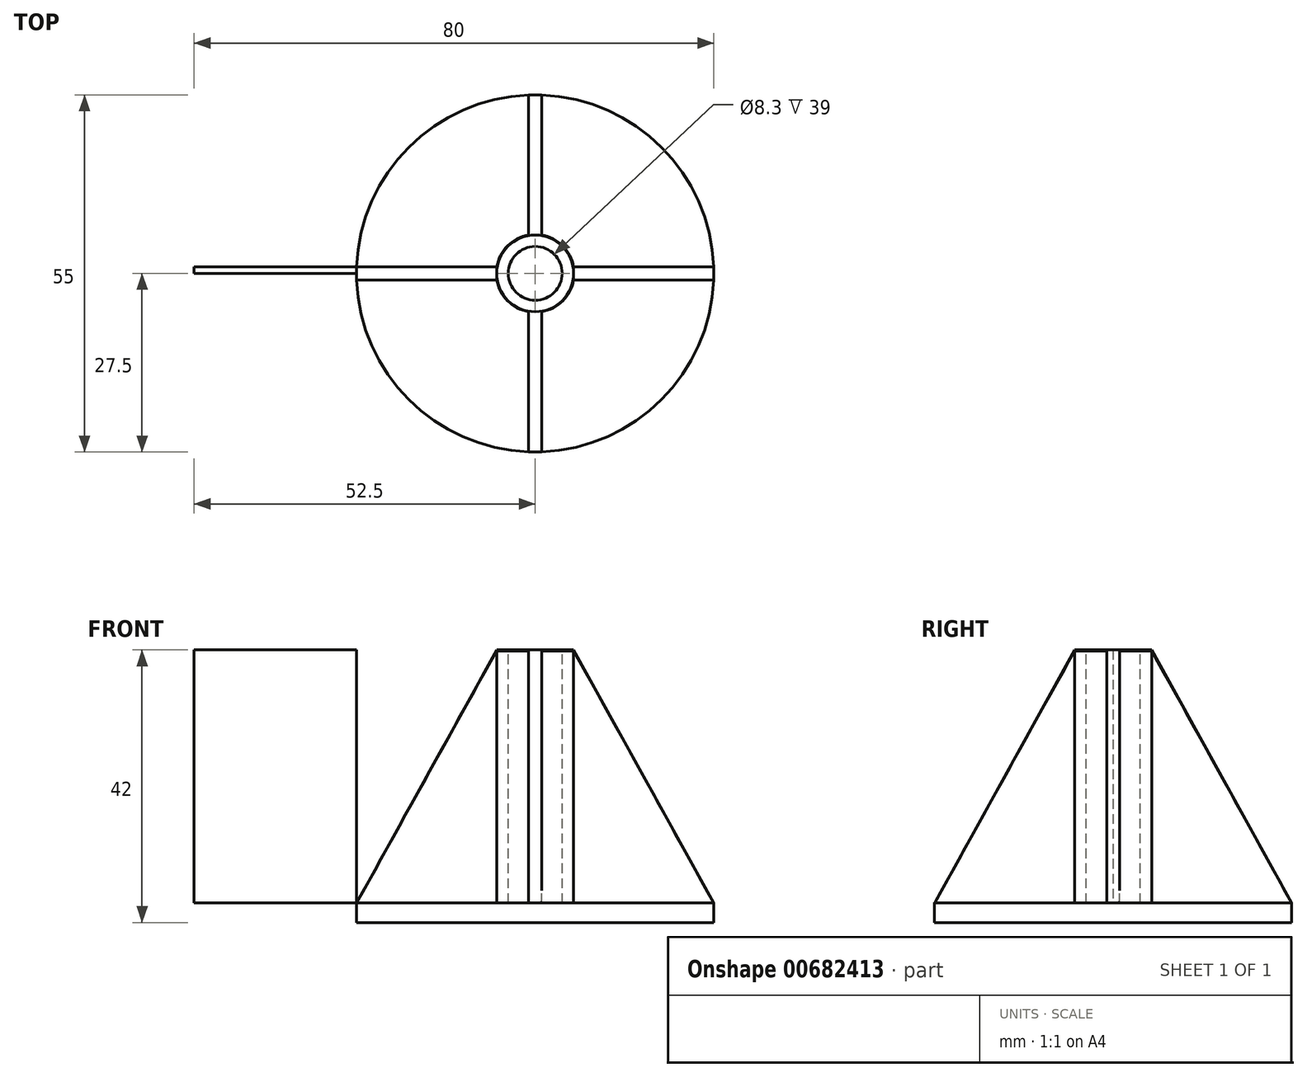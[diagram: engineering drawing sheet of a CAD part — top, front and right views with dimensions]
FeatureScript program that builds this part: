
annotation { "Feature Type Name" : "Feature", "Feature Type Description" : "" }
export const myFeature = defineFeature(function(context is Context, id is Id, definition is map)
    precondition{}
    {
        {
            var Q0;
            Q0=qCreatedBy(makeId("Top.planeOp"),FACE);
            var sketch = newSketch(context, id + "F0", { "sketchPlane" : qUnion([Q0])});
            skCircle(sketch, "E0", {"center": v(-3.3, 0) * mm, "radius": 27.5 * mm});
            skCircle(sketch, "E1", {"center": v(-3.3, 0) * mm, "radius": 26.5 * mm});
            skSolve(sketch);
        }
        {
            var Q0;
            Q0 = qSketchRegion(id + "F0", true);
            extrude(context, id + "F1", {"entities" : qUnion([Q0]), "depth" : 10 * mm, "offsetDistance" : 25 * mm});
        }
        {
            var Q0;
            Q0=makeQuery(id+"F1.opExtrude","CAP_FACE",FACE,{"disambiguationData":[OSD([sQuery(id+"F0.wireOp",EDGE,"E0"),sQuery(id+"F0.wireOp",EDGE,"E1")])],"isStart":false});
            var sketch = newSketch(context, id + "F2", { "sketchPlane" : qUnion([Q0])});
            skLineSegment(sketch, "E2", {"start": v(-30.8, 0) * mm, "end": v(24.2, 0) * mm});
            skCircle(sketch, "E3", {"center": v(-3.3, 0) * mm, "radius": 27.5 * mm});
            skSolve(sketch);
        }
        {
            var Q0;
            Q0 = qSketchRegion(id + "F2", true);
            extrude(context, id + "F3", {"entities" : qUnion([Q0]), "operationType" : NewBodyOperationType.ADD, "depth" : 3 * mm, "offsetDistance" : 25 * mm});
        }
        {
            var Q0;
            Q0=makeQuery(id+"F3.opExtrude","CAP_FACE",FACE,{"disambiguationData":[OSD([sQuery(id+"F2.wireOp",EDGE,"E3")])],"isStart":false});
            var sketch = newSketch(context, id + "F4", { "sketchPlane" : qUnion([Q0])});
            skCircle(sketch, "E4", {"center": v(-3.3, 0) * mm, "radius": 6 * mm});
            skSolve(sketch);
        }
        {
            var Q0;
            Q0 = qSketchRegion(id + "F4", true);
            extrude(context, id + "F5", {"entities" : qUnion([Q0]), "operationType" : NewBodyOperationType.ADD, "depth" : 39 * mm, "offsetDistance" : 25 * mm});
        }
        {
            var Q0;
            Q0=makeQuery(id+"F5.opExtrude","CAP_FACE",FACE,{"disambiguationData":[OSD([sQuery(id+"F4.wireOp",EDGE,"E4")])],"isStart":false});
            var sketch = newSketch(context, id + "F6", { "sketchPlane" : qUnion([Q0])});
            skCircle(sketch, "E5", {"center": v(-3.3, 0) * mm, "radius": 4.15 * mm});
            skSolve(sketch);
        }
        {
            var Q0;
            Q0 = qSketchRegion(id + "F6", true);
            extrude(context, id + "F7", {"entities" : qUnion([Q0]), "operationType" : NewBodyOperationType.REMOVE, "oppositeDirection" : true, "depth" : 39 * mm, "offsetDistance" : 25 * mm});
        }
        {
            var Q0;
            Q0=makeQuery(id+"F3.opExtrude","CAP_FACE",FACE,{"disambiguationData":[OSD([sQuery(id+"F2.wireOp",EDGE,"E3")])],"isStart":false});
            var sketch = newSketch(context, id + "F8", { "sketchPlane" : qUnion([Q0])});
            skLineSegment(sketch, "E6", {"start": v(-3.3, 0) * mm, "end": v(-3.3, -27.5) * mm});
            skLineSegment(sketch, "E7", {"start": v(-3.3, -27.5) * mm, "end": v(-2.3, -27.5) * mm});
            skLineSegment(sketch, "E8", {"start": v(-2.3, -27.5) * mm, "end": v(-2.3, -5.14) * mm});
            skLineSegment(sketch, "E9", {"start": v(-2.3, -5.14) * mm, "end": v(-4.3, -5.14) * mm});
            skLineSegment(sketch, "E10", {"start": v(-4.3, -5.14) * mm, "end": v(-4.3, -27.48) * mm});
            skLineSegment(sketch, "E11", {"start": v(-4.3, -27.48) * mm, "end": v(-3.3, -27.5) * mm});
            skLineSegment(sketch, "E12.1.0", {"start": v(24.2, 1) * mm, "end": v(1.83, 1) * mm});
            skLineSegment(sketch, "E12.1.1", {"start": v(1.83, 1) * mm, "end": v(1.83, -1) * mm});
            skLineSegment(sketch, "E12.1.2", {"start": v(1.83, -1) * mm, "end": v(24.17, -1) * mm});
            skLineSegment(sketch, "E12.1.3", {"start": v(24.17, -1) * mm, "end": v(24.2, 0) * mm});
            skLineSegment(sketch, "E12.1.4", {"start": v(24.2, 0) * mm, "end": v(24.2, 1) * mm});
            skLineSegment(sketch, "E12.2.0", {"start": v(-4.3, 27.5) * mm, "end": v(-4.3, 5.14) * mm});
            skLineSegment(sketch, "E12.2.1", {"start": v(-4.3, 5.14) * mm, "end": v(-2.3, 5.14) * mm});
            skLineSegment(sketch, "E12.2.2", {"start": v(-2.3, 5.14) * mm, "end": v(-2.3, 27.48) * mm});
            skLineSegment(sketch, "E12.2.3", {"start": v(-2.3, 27.48) * mm, "end": v(-3.3, 27.5) * mm});
            skLineSegment(sketch, "E12.2.4", {"start": v(-3.3, 27.5) * mm, "end": v(-4.3, 27.5) * mm});
            skLineSegment(sketch, "E12.3.0", {"start": v(-30.8, -1) * mm, "end": v(-8.45, -1) * mm});
            skLineSegment(sketch, "E12.3.1", {"start": v(-8.45, -1) * mm, "end": v(-8.45, 1) * mm});
            skLineSegment(sketch, "E12.3.2", {"start": v(-8.45, 1) * mm, "end": v(-30.8, 1) * mm});
            skLineSegment(sketch, "E12.3.3", {"start": v(-30.8, 1) * mm, "end": v(-30.8, 0) * mm});
            skLineSegment(sketch, "E12.3.4", {"start": v(-30.8, 0) * mm, "end": v(-30.8, -1) * mm});
            skPoint(sketch, "E12.center", {"position": v(-3.3, 0) * mm});
            skSolve(sketch);
        }
        {
            var Q0;
            Q0 = qSketchRegion(id + "F8", true);
            extrude(context, id + "F9", {"entities" : qUnion([Q0]), "operationType" : NewBodyOperationType.ADD, "depth" : 39 * mm, "offsetDistance" : 25 * mm});
        }
        {
            var Q0;
            Q0=makeQuery(id+"F9.opExtrude","SWEPT_FACE",FACE,{"disambiguationData":[OSD([sQuery(id+"F8.wireOp",EDGE,"E12.3.4")])]});
            var sketch = newSketch(context, id + "F10", { "sketchPlane" : qUnion([Q0])});
            skLineSegment(sketch, "E13", {"start": v(0, 52) * mm, "end": v(0, 13) * mm});
            skLineSegment(sketch, "E14", {"start": v(0, 13) * mm, "end": v(-0.99, 13) * mm});
            skLineSegment(sketch, "E15", {"start": v(-0.99, 13) * mm, "end": v(-0.99, 52) * mm});
            skLineSegment(sketch, "E16", {"start": v(-0.99, 52) * mm, "end": v(0, 52) * mm});
            skSolve(sketch);
        }
        {
            var Q0;
            Q0 = qSketchRegion(id + "F10", true);
            extrude(context, id + "F11", {"entities" : qUnion([Q0]), "depth" : 25 * mm, "offsetDistance" : 25 * mm});
        }
        {
            var Q0;
            Q0=makeQuery(id+"F11.opExtrude","SWEPT_FACE",FACE,{"disambiguationData":[OSD([sQuery(id+"F10.wireOp",EDGE,"E13")])]});
            var sketch = newSketch(context, id + "F12", { "sketchPlane" : qUnion([Q0])});
            skLineSegment(sketch, "E17", {"start": v(-30.8, 13) * mm, "end": v(24.2, 13) * mm});
            skLineSegment(sketch, "E18", {"start": v(24.2, 13) * mm, "end": v(32.46, 54.61) * mm});
            skLineSegment(sketch, "E19", {"start": v(32.46, 54.61) * mm, "end": v(1.97, 54.61) * mm});
            skLineSegment(sketch, "E20", {"start": v(1.97, 54.61) * mm, "end": v(2.6, 52) * mm});
            skLineSegment(sketch, "E21", {"start": v(2.6, 52) * mm, "end": v(24.2, 13) * mm});
            skLineSegment(sketch, "E22", {"start": v(-3.3, 13) * mm, "end": v(-3.3, 60.1) * mm});
            skSolve(sketch);
        }
        {
            var Q0;
            Q0=makeQuery(id+"F12.imprint","IMPRINT",FACE,{"disambiguationData":[TD([[makeQuery(id+"F12.imprint","IMPRINT",EDGE,{"derivedFrom":sQuery(id+"F12.wireOp",EDGE,"E18")}),1.0]])]});
            var Q1;
            Q1=sQuery(id+"F12.wireOp",EDGE,"E22");
            revolve(context, id + "F13", {"entities" : qUnion([Q0]), "axis" : qUnion([Q1]), "revolveType" : RevolveType.FULL});
        }
        {
            var Q0;
            Q0=makeQuery(id+"F13.opRevolve","SWEPT_BODY",BODY,{"disambiguationData":[OSD([sQuery(id+"F12.wireOp",EDGE,"E18"),sQuery(id+"F12.wireOp",EDGE,"E19"),sQuery(id+"F12.wireOp",EDGE,"E20"),sQuery(id+"F12.wireOp",EDGE,"E21")])]});
            var Q1;
            Q1=makeQuery(id+"F1.opExtrude","SWEPT_BODY",BODY,{"disambiguationData":[OSD([sQuery(id+"F0.wireOp",EDGE,"E0"),sQuery(id+"F0.wireOp",EDGE,"E1")])]});
            booleanBodies(context, id + "F14", {"operationType" : BooleanOperationType.SUBTRACTION, "tools" : qUnion([Q0]), "targets" : qUnion([Q1])});
        }
        {
            var Q0;
            Q0=makeQuery(id+"F3.opExtrude","CAP_FACE",FACE,{"disambiguationData":[OSD([sQuery(id+"F2.wireOp",EDGE,"E3")])],"isStart":true});
            var sketch = newSketch(context, id + "F15", { "sketchPlane" : qUnion([Q0])});
            skCircle(sketch, "E23", {"center": v(-3.3, 0) * mm, "radius": 61.15 * mm});
            skSolve(sketch);
        }
        {
            var Q0;
            Q0 = qSketchRegion(id + "F15", true);
            extrude(context, id + "F16", {"entities" : qUnion([Q0]), "operationType" : NewBodyOperationType.REMOVE, "depth" : 40 * mm, "offsetDistance" : 25 * mm});
        }
    });
